# Revit family: Luca_Tables_Laptop
name_source: partatom
category: Furniture
revit_build: Autodesk Revit 2016 (Build: 20150714_1515(x64)
units: mm (PartAtom-declared; Revit-internal decimal feet)

## family parameters
Always vertical = Yes
Cut with Voids When Loaded = No
OmniClass Number = 23.40.20.00
OmniClass Title = General Furniture and Specialties
Room Calculation Point = No
Shared = No
Work Plane-Based = No

## types (6) — shared parameters
Manufacturer = Bernhardt Design
Model = Luca
URL = http://www.bernhardtdesign.com

## per-type parameters (varying)
| type | Catalog | SKU |
| Luca - Table - LUS-LDTOAKBK | LUS-LDTOAKBK | LUS-LDTOAKBK |
| Luca - Table - LUS-LDTOAKPA | LUS-LDTOAKPA | LUS-LDTOAKPA |
| Luca - Table - LUS-LDTOAKWH | LUS-LDTOAKWH | LUS-LDTOAKWH |
| Luca - Table - LUS-LDTWLTBK | LUS-LDTWLTBK | LUS-LDTWLTBK |
| Luca - Table - LUS-LDTWLTPA | LUS-LDTWLTPA | LUS-LDTWLTPA |
| Luca - Table - LUS-LDTWLTWH | LUS-LDTWLTWH | LUS-LDTWLTWH |

## geometry (parser evidence)
native form markers: Sweep x5
no freeform markers — native parametric forms only
